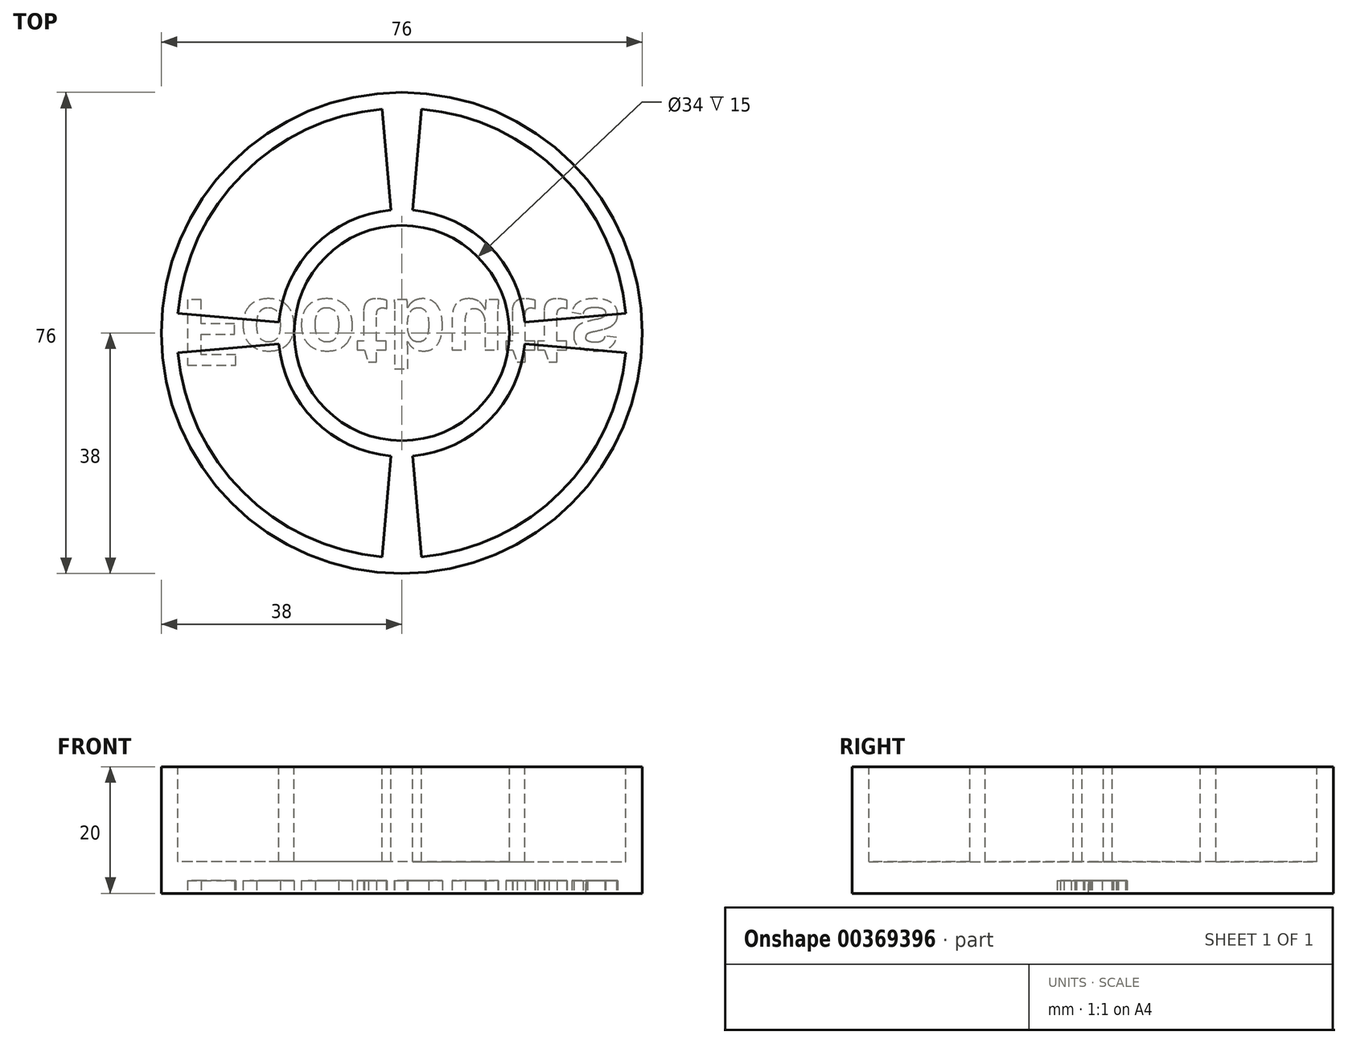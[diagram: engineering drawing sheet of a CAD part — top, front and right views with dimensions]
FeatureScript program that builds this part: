
annotation { "Feature Type Name" : "Feature", "Feature Type Description" : "" }
export const myFeature = defineFeature(function(context is Context, id is Id, definition is map)
    precondition{}
    {
        {
            var Q0;
            Q0=qCreatedBy(makeId("Top.planeOp"),FACE);
            var sketch = newSketch(context, id + "F0", { "sketchPlane" : qUnion([Q0])});
            skCircle(sketch, "E0", {"center": v(0, 0) * mm, "radius": 38 * mm});
            skSolve(sketch);
        }
        {
            var Q0;
            Q0=makeQuery(id+"F0.imprint","IMPRINT",FACE,{"disambiguationData":[TD([[makeQuery(id+"F0.imprint","IMPRINT",EDGE,{"derivedFrom":sQuery(id+"F0.wireOp",EDGE,"E0")}),1.0]])]});
            extrude(context, id + "F1", {"entities" : qUnion([Q0]), "depth" : 20 * mm});
        }
        {
            var Q0;
            Q0=makeQuery(id+"F1.opExtrude","CAP_FACE",FACE,{"disambiguationData":[OSD([sQuery(id+"F0.wireOp",EDGE,"E0")])],"isStart":false});
            var sketch = newSketch(context, id + "F2", { "sketchPlane" : qUnion([Q0])});
            skArc(sketch, "E1", {"start": v(-3.1, 35.36) * mm, "mid": v(-25.1, 25.1) * mm, "end": v(-35.36, 3.1) * mm});
            skCircle(sketch, "E2", {"center": v(0, 0) * mm, "radius": 17 * mm});
            skArc(sketch, "E3", {"start": v(-1.7, 19.43) * mm, "mid": v(-13.79, 13.79) * mm, "end": v(-19.43, 1.7) * mm});
            skLineSegment(sketch, "E4", {"start": v(0, -35.5) * mm, "end": v(0, 35.5) * mm, "construction": true});
            skLineSegment(sketch, "E5", {"start": v(35.5, 0) * mm, "end": v(-35.5, 0) * mm, "construction": true});
            skLineSegment(sketch, "E6", {"start": v(1.7, 19.43) * mm, "end": v(3.1, 35.36) * mm});
            skLineSegment(sketch, "E7", {"start": v(-1.7, 19.43) * mm, "end": v(-3.1, 35.36) * mm});
            skLineSegment(sketch, "E8", {"start": v(-19.43, -1.7) * mm, "end": v(-35.36, -3.1) * mm});
            skLineSegment(sketch, "E9", {"start": v(-19.43, 1.7) * mm, "end": v(-35.36, 3.1) * mm});
            skArc(sketch, "E10.trimOffspring", {"start": v(35.36, 3.1) * mm, "mid": v(25.1, 25.1) * mm, "end": v(3.1, 35.36) * mm});
            skArc(sketch, "E11.trimOffspring", {"start": v(3.1, -35.36) * mm, "mid": v(25.1, -25.1) * mm, "end": v(35.36, -3.1) * mm});
            skArc(sketch, "E12.trimOffspring", {"start": v(-35.36, -3.1) * mm, "mid": v(-25.1, -25.1) * mm, "end": v(-3.1, -35.36) * mm});
            skLineSegment(sketch, "E13.trimOffspring", {"start": v(19.43, 1.7) * mm, "end": v(35.36, 3.1) * mm});
            skLineSegment(sketch, "E14.trimOffspring", {"start": v(19.43, -1.7) * mm, "end": v(35.36, -3.1) * mm});
            skArc(sketch, "E15.trimOffspring", {"start": v(19.43, 1.7) * mm, "mid": v(13.79, 13.79) * mm, "end": v(1.7, 19.43) * mm});
            skLineSegment(sketch, "E16.trimOffspring", {"start": v(1.7, -19.43) * mm, "end": v(3.1, -35.36) * mm});
            skLineSegment(sketch, "E17.trimOffspring", {"start": v(-1.7, -19.43) * mm, "end": v(-3.1, -35.36) * mm});
            skArc(sketch, "E18.trimOffspring", {"start": v(1.7, -19.43) * mm, "mid": v(13.79, -13.79) * mm, "end": v(19.43, -1.7) * mm});
            skArc(sketch, "E19.trimOffspring", {"start": v(-19.43, -1.7) * mm, "mid": v(-13.79, -13.79) * mm, "end": v(-1.7, -19.43) * mm});
            skSolve(sketch);
        }
        {
            var Q0;
            Q0=makeQuery(id+"F2.imprint","IMPRINT",FACE,{"disambiguationData":[TD([[makeQuery(id+"F2.imprint","IMPRINT",EDGE,{"derivedFrom":sQuery(id+"F2.wireOp",EDGE,"E1")}),1.0]])]});
            var Q1;
            Q1=makeQuery(id+"F2.imprint","IMPRINT",FACE,{"disambiguationData":[TD([[makeQuery(id+"F2.imprint","IMPRINT",EDGE,{"derivedFrom":sQuery(id+"F2.wireOp",EDGE,"E6")}),-1.0]])]});
            var Q2;
            Q2=makeQuery(id+"F2.imprint","IMPRINT",FACE,{"disambiguationData":[TD([[makeQuery(id+"F2.imprint","IMPRINT",EDGE,{"derivedFrom":sQuery(id+"F2.wireOp",EDGE,"E8")}),1.0]])]});
            var Q3;
            Q3=makeQuery(id+"F2.imprint","IMPRINT",FACE,{"disambiguationData":[TD([[makeQuery(id+"F2.imprint","IMPRINT",EDGE,{"derivedFrom":sQuery(id+"F2.wireOp",EDGE,"E11.trimOffspring")}),1.0]])]});
            var Q4;
            Q4=makeQuery(id+"F2.imprint","IMPRINT",FACE,{"disambiguationData":[TD([[makeQuery(id+"F2.imprint","IMPRINT",EDGE,{"derivedFrom":sQuery(id+"F2.wireOp",EDGE,"E2")}),1.0]])]});
            extrude(context, id + "F3", {"entities" : qUnion([Q0, Q1, Q2, Q3, Q4]), "operationType" : NewBodyOperationType.REMOVE, "oppositeDirection" : true, "depth" : 15 * mm});
        }
        {
            var Q0;
            Q0=makeQuery(id+"F1.opExtrude","CAP_FACE",FACE,{"disambiguationData":[OSD([sQuery(id+"F0.wireOp",EDGE,"E0")])],"isStart":true});
            var sketch = newSketch(context, id + "F4", { "sketchPlane" : qUnion([Q0])});
            skText(sketch, "E20", { "text": "Footbutts\n", "fontName": "Arimo-Bold.ttf"});
            const initialGuessF4  = {"E20": [-0.03488, -0.00528, 1, 0, 0.01087]};
            skSetInitialGuess(sketch, initialGuessF4);
            skSolve(sketch);
        }
        {
            var Q0;
            Q0=qSketchRegion(id+"F4",true);
            extrude(context, id + "F5", {"entities" : qUnion([Q0]), "operationType" : NewBodyOperationType.REMOVE, "oppositeDirection" : true, "depth" : 2 * mm});
        }
    });
